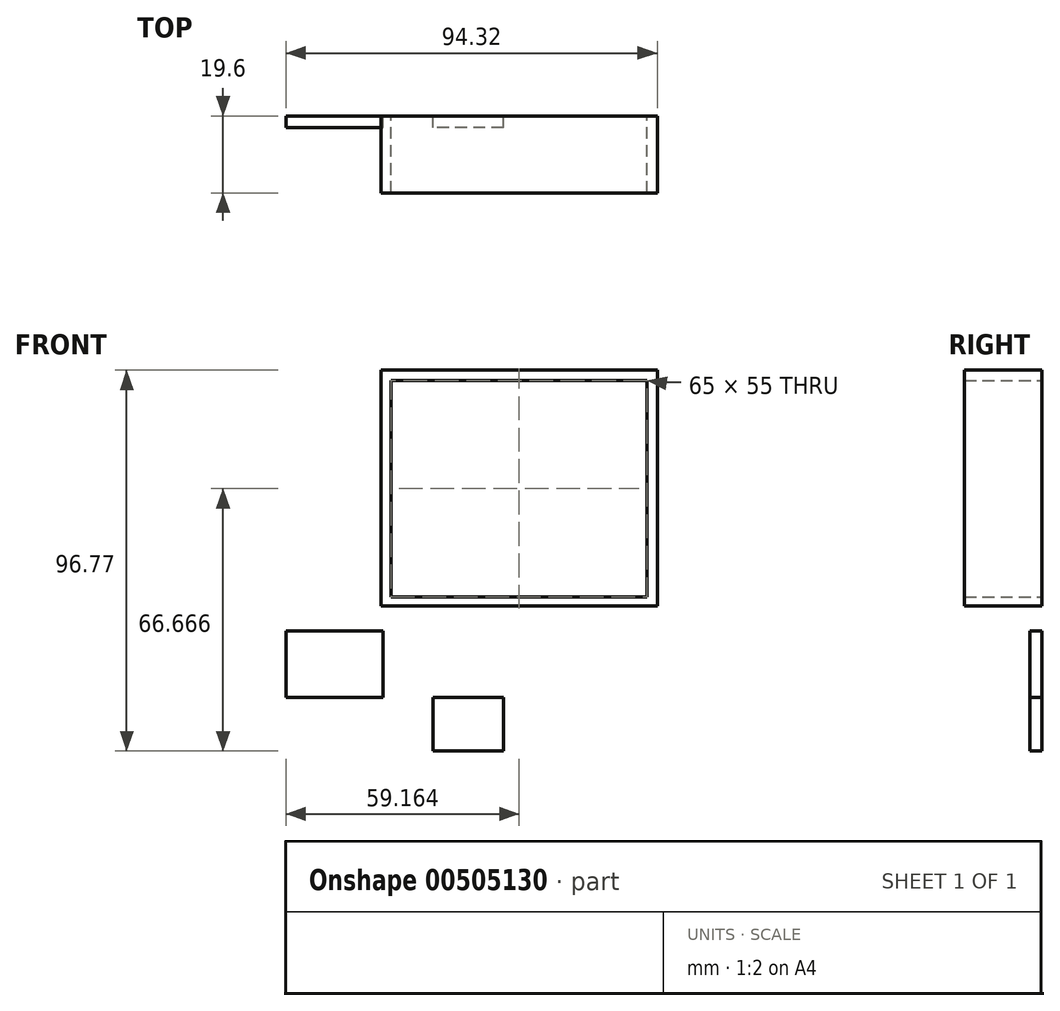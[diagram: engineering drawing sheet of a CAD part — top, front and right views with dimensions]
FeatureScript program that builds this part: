
annotation { "Feature Type Name" : "Feature", "Feature Type Description" : "" }
export const myFeature = defineFeature(function(context is Context, id is Id, definition is map)
    precondition{}
    {
        {
            var Q0;
            Q0=qCreatedBy(makeId("Front.planeOp"),FACE);
            var sketch = newSketch(context, id + "F0", { "sketchPlane" : qUnion([Q0])});
            skLineSegment(sketch, "E0.bottom", {"start": v(-34, 28.03) * mm, "end": v(31, 28.03) * mm});
            skLineSegment(sketch, "E0.top", {"start": v(-34, -26.97) * mm, "end": v(31, -26.97) * mm});
            skLineSegment(sketch, "E0.left", {"start": v(-34, 28.03) * mm, "end": v(-34, -26.97) * mm});
            skLineSegment(sketch, "E0.right", {"start": v(31, 28.03) * mm, "end": v(31, -26.97) * mm});
            skLineSegment(sketch, "E1.bottom", {"start": v(-3.16, -8.28) * mm, "end": v(16.84, -8.28) * mm});
            skLineSegment(sketch, "E1.top", {"start": v(-3.16, 11.72) * mm, "end": v(16.84, 11.72) * mm});
            skLineSegment(sketch, "E1.left", {"start": v(-3.16, -8.28) * mm, "end": v(-3.16, 11.72) * mm});
            skLineSegment(sketch, "E1.right", {"start": v(16.84, -8.28) * mm, "end": v(16.84, 11.72) * mm});
            skLineSegment(sketch, "E2.bottom", {"start": v(-36.55, 30.63) * mm, "end": v(33.66, 30.63) * mm});
            skLineSegment(sketch, "E2.top", {"start": v(-36.55, -29.32) * mm, "end": v(33.66, -29.32) * mm});
            skLineSegment(sketch, "E2.left", {"start": v(-36.55, 30.63) * mm, "end": v(-36.55, -29.32) * mm});
            skLineSegment(sketch, "E2.right", {"start": v(33.66, 30.63) * mm, "end": v(33.66, -29.32) * mm});
            skSolve(sketch);
        }
        {
            var Q0;
            Q0 = qSketchRegion(id + "F0", true);
            extrude(context, id + "F1", {"entities" : qUnion([Q0]), "depth" : 19.6 * mm});
        }
        {
            var Q0;
            Q0=qCreatedBy(makeId("Front.planeOp"),FACE);
            var sketch = newSketch(context, id + "F2", { "sketchPlane" : qUnion([Q0])});
            skLineSegment(sketch, "E3.bottom", {"start": v(-60.66, -35.6) * mm, "end": v(-36.04, -35.6) * mm});
            skLineSegment(sketch, "E3.top", {"start": v(-60.66, -52.5) * mm, "end": v(-36.04, -52.5) * mm});
            skLineSegment(sketch, "E3.left", {"start": v(-60.66, -35.6) * mm, "end": v(-60.66, -52.5) * mm});
            skLineSegment(sketch, "E3.right", {"start": v(-36.04, -35.6) * mm, "end": v(-36.04, -52.5) * mm});
            skLineSegment(sketch, "E4.bottom", {"start": v(-5.49, -52.5) * mm, "end": v(-23.28, -52.5) * mm});
            skLineSegment(sketch, "E4.top", {"start": v(-5.49, -66.14) * mm, "end": v(-23.28, -66.14) * mm});
            skLineSegment(sketch, "E4.left", {"start": v(-5.49, -52.5) * mm, "end": v(-5.49, -66.14) * mm});
            skLineSegment(sketch, "E4.right", {"start": v(-23.28, -52.5) * mm, "end": v(-23.28, -66.14) * mm});
            skSolve(sketch);
        }
        {
            var Q0;
            Q0 = qSketchRegion(id + "F2", true);
            extrude(context, id + "F3", {"entities" : qUnion([Q0]), "depth" : 3 * mm, "offsetDistance" : 25 * mm});
        }
    });
